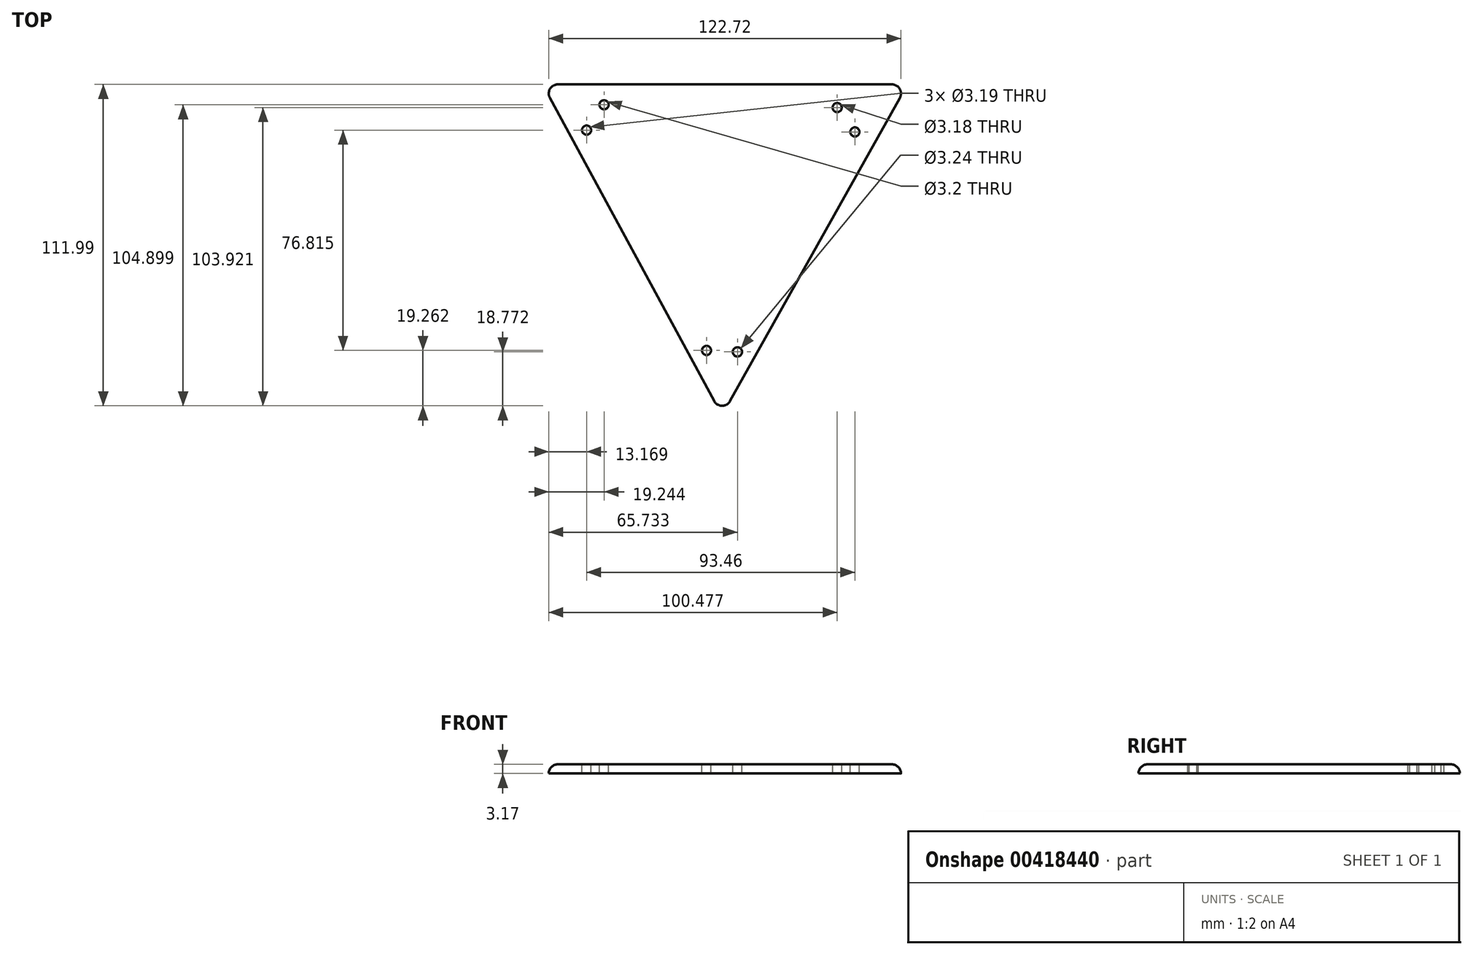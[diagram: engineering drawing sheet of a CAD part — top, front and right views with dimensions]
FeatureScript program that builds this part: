
annotation { "Feature Type Name" : "Feature", "Feature Type Description" : "" }
export const myFeature = defineFeature(function(context is Context, id is Id, definition is map)
    precondition{}
    {
        {
            var Q0;
            Q0=qCreatedBy(makeId("Front.planeOp"),FACE);
            var sketch = newSketch(context, id + "F0", { "sketchPlane" : qUnion([Q0])});
            skLineSegment(sketch, "E0", {"start": v(-62.51, 39.64) * mm, "end": v(64.6, 39.64) * mm});
            skLineSegment(sketch, "E1", {"start": v(64.6, 39.64) * mm, "end": v(0, -75.77) * mm});
            skLineSegment(sketch, "E2", {"start": v(-62.51, 39.64) * mm, "end": v(0, -75.77) * mm});
            skCircle(sketch, "E3", {"center": v(-41.1, 32.54) * mm, "radius": 1.6 * mm});
            skCircle(sketch, "E4", {"center": v(-47.18, 23.72) * mm, "radius": 1.6 * mm});
            skCircle(sketch, "E5", {"center": v(46.28, 23.1) * mm, "radius": 1.6 * mm});
            skCircle(sketch, "E6", {"center": v(5.38, -53.58) * mm, "radius": 1.62 * mm});
            skCircle(sketch, "E7", {"center": v(40.13, 31.56) * mm, "radius": 1.59 * mm});
            skCircle(sketch, "E8", {"center": v(7.83, 33.52) * mm, "radius": 1.58 * mm});
            skCircle(sketch, "E9", {"center": v(-5.38, -53.1) * mm, "radius": 1.6 * mm});
            skCircle(sketch, "E10", {"center": v(-6.85, 33.52) * mm, "radius": 1.57 * mm});
            skSolve(sketch);
        }
        {
            var Q0;
            Q0=qSketchRegion(id+"F0",true);
            var Q1;
            Q1=makeQuery(id+"F0.imprint","IMPRINT",FACE,{"disambiguationData":[TD([[makeQuery(id+"F0.imprint","IMPRINT",EDGE,{"derivedFrom":sQuery(id+"F0.wireOp",EDGE,"E8")}),1.0]])]});
            var Q2;
            Q2=makeQuery(id+"F0.imprint","IMPRINT",FACE,{"disambiguationData":[TD([[makeQuery(id+"F0.imprint","IMPRINT",EDGE,{"derivedFrom":sQuery(id+"F0.wireOp",EDGE,"E10")}),1.0]])]});
            extrude(context, id + "F1", {"entities" : qUnion([Q0, Q1, Q2]), "oppositeDirection" : true, "depth" : 3.17 * mm});
        }
        {
            var Q0;
            Q0=makeQuery(id+"F1.opExtrude","SWEPT_EDGE",EDGE,{"disambiguationData":[OSD([sQuery(id+"F0.wireOp",EDGE,"E0"),sQuery(id+"F0.wireOp",EDGE,"E1")])]});
            var Q1;
            Q1=makeQuery(id+"F1.opExtrude","SWEPT_EDGE",EDGE,{"disambiguationData":[OSD([sQuery(id+"F0.wireOp",EDGE,"E0"),sQuery(id+"F0.wireOp",EDGE,"E2")])]});
            var Q2;
            Q2=makeQuery(id+"F1.opExtrude","SWEPT_EDGE",EDGE,{"disambiguationData":[OSD([sQuery(id+"F0.wireOp",EDGE,"E1"),sQuery(id+"F0.wireOp",EDGE,"E2")])]});
            var Q3;
            Q3=makeQuery(id+"F1.opExtrude","CAP_EDGE",EDGE,{"disambiguationData":[OSD([sQuery(id+"F0.wireOp",EDGE,"E2")])],"isStart":true});
            var Q4;
            Q4=makeQuery(id+"F1.opExtrude","CAP_EDGE",EDGE,{"disambiguationData":[OSD([sQuery(id+"F0.wireOp",EDGE,"E1")])],"isStart":true});
            var Q5;
            Q5=makeQuery(id+"F1.opExtrude","CAP_EDGE",EDGE,{"disambiguationData":[OSD([sQuery(id+"F0.wireOp",EDGE,"E0")])],"isStart":true});
            fillet(context, id + "F2", {"entities" : qUnion([Q0, Q1, Q2, Q3, Q4, Q5]), "radius" : 3.17 * mm, "tangentPropagation" : true, "allowEdgeOverflow" : false});
        }
        {
            var Q0;
            Q0=makeQuery(id+"F1.opExtrude","SWEPT_BODY",BODY,{"disambiguationData":[OSD([sQuery(id+"F0.wireOp",EDGE,"E0"),sQuery(id+"F0.wireOp",EDGE,"E1"),sQuery(id+"F0.wireOp",EDGE,"E2"),sQuery(id+"F0.wireOp",EDGE,"E3"),sQuery(id+"F0.wireOp",EDGE,"E4"),sQuery(id+"F0.wireOp",EDGE,"E5"),sQuery(id+"F0.wireOp",EDGE,"E6"),sQuery(id+"F0.wireOp",EDGE,"E7"),sQuery(id+"F0.wireOp",EDGE,"E9")])]});
            var Q1;
            {var subQ0=sQuery(id+"F0.wireOp",EDGE,"E0");Q1=makeQuery(id+"F2.opFillet","BLEND_EDGE",EDGE,{"blendedFrom":[makeQuery(id+"F1.opExtrude","CAP_EDGE",EDGE,{"disambiguationData":[OSD([subQ0])],"isStart":true}),makeQuery(id+"F1.opExtrude","CAP_FACE",FACE,{"disambiguationData":[OSD([subQ0,sQuery(id+"F0.wireOp",EDGE,"E1"),sQuery(id+"F0.wireOp",EDGE,"E2"),sQuery(id+"F0.wireOp",EDGE,"E3"),sQuery(id+"F0.wireOp",EDGE,"E4"),sQuery(id+"F0.wireOp",EDGE,"E5"),sQuery(id+"F0.wireOp",EDGE,"E6"),sQuery(id+"F0.wireOp",EDGE,"E7"),sQuery(id+"F0.wireOp",EDGE,"E9")])],"isStart":false})],"blendedInto":[makeQuery(id+"F1.opExtrude","CAP_FACE",FACE,{"disambiguationData":[OSD([subQ0,sQuery(id+"F0.wireOp",EDGE,"E1"),sQuery(id+"F0.wireOp",EDGE,"E2"),sQuery(id+"F0.wireOp",EDGE,"E3"),sQuery(id+"F0.wireOp",EDGE,"E4"),sQuery(id+"F0.wireOp",EDGE,"E5"),sQuery(id+"F0.wireOp",EDGE,"E6"),sQuery(id+"F0.wireOp",EDGE,"E7"),sQuery(id+"F0.wireOp",EDGE,"E9")])],"isStart":false})]});}
            transform(context, id + "F3", {"entities" : qUnion([Q0]), "transformType" : TransformType.ROTATION, "transformAxis" : qUnion([Q1]), "angle" : 90 * degree, "oppositeDirection" : true, "makeCopy" : false});
        }
    });
